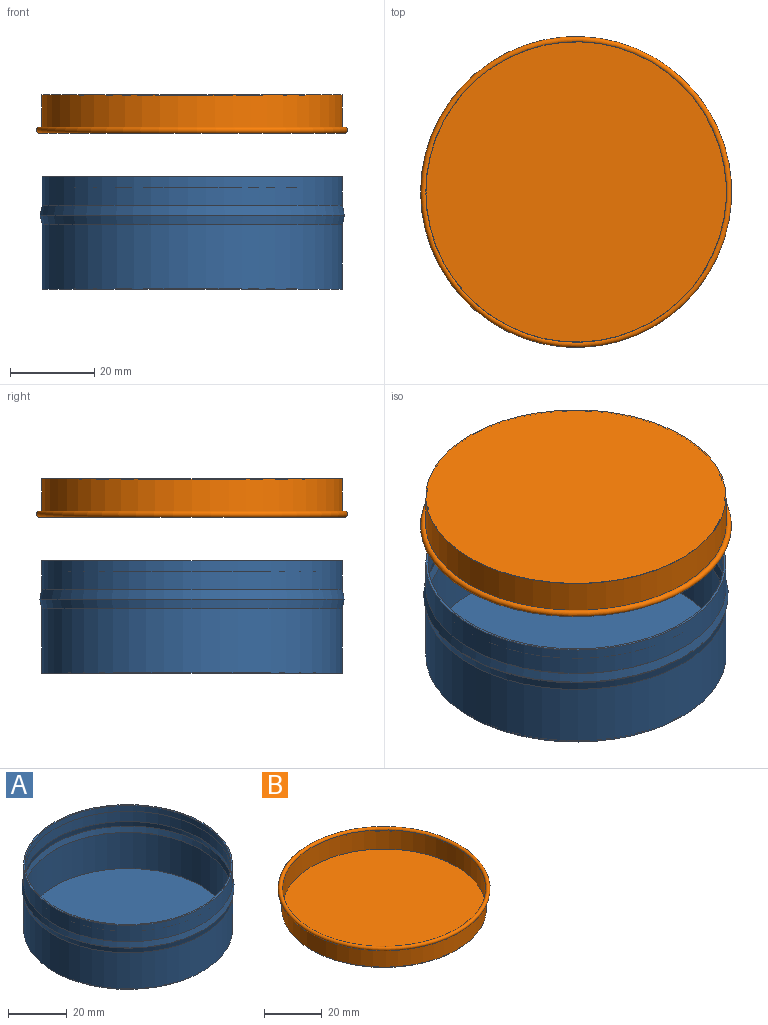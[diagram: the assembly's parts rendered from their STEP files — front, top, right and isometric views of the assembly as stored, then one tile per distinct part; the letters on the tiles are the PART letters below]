
ASSEMBLY  parts=2 mates=1
PART A: 13 faces, bbox 72.1x72.1x26.7 mm
  f0: cylinder r=35.56mm len=71.12mm, axis (0,0,1), area 3405.1mm2, adj f1,f12
  f1: plane 71.12x71.12mm, normal (0,0,-1), area 3972.6mm2, adj f0
  f2: plane 70.61x70.61mm, normal (0,0,1), area 3916mm2, adj f3
  f3: cylinder r=35.31mm len=70.61mm, axis (0,0,1), area 3324.4mm2, adj f2,f4
  f4: cone r=35.31mm half-angle=12.5deg, axis (0,0,1), area 523.2mm2, adj f3,f5
  f5: cone r=35.81mm half-angle=12.5deg, axis (0,0,-1), area 523.2mm2, adj f4,f6
  f6: cylinder r=35.31mm len=70.61mm, axis (0,0,1), area 957.9mm2, adj f5,f7
  f7: cone r=35.31mm half-angle=63.4deg, axis (0,0,-1), area 62.8mm2, adj f6,f8
  f8: cylinder r=35.05mm len=70.1mm, axis (0,0,1), area 531.4mm2, adj f7,f9
  f9: plane 71.12x71.12mm, normal (0,0,1), area 112.7mm2, adj f8,f10
  f10: cylinder r=35.56mm len=71.12mm, axis (0,0,1), area 1532.3mm2, adj f9,f11
  f11: cone r=36.07mm half-angle=12.5deg, axis (0,0,-1), area 527mm2, adj f10,f12
  f12: cone r=35.56mm half-angle=12.5deg, axis (0,0,1), area 527mm2, adj f0,f11
PART B: 7 faces, bbox 79.7x79.7x8.4 mm
  f0: cylinder r=35.56mm len=71.12mm, axis (0,0,1), area 1872.8mm2, adj f1,f6
  f1: plane 71.12x71.12mm, normal (0,0,-1), area 3972.6mm2, adj f0
  f2: plane 70.61x70.61mm, normal (0,0,1), area 3916mm2, adj f3
  f3: cylinder r=35.31mm len=70.61mm, axis (0,0,1), area 1803.1mm2, adj f2,f4
  f4: torus R=36.07mm, axis (0,0,1), area 930.7mm2, adj f3,f5
  f5: cone r=35.6mm half-angle=37.8deg, axis (0,0,1), area 56.9mm2, adj f4,f6
  f6: torus R=36.07mm, axis (0,0,1), area 619.8mm2, adj f0,f5
PLACE A t=(-13.33,10.17,-2.97)mm
PLACE B rot(axis=(0,1,0),180deg) t=(-13.33,10.17,43.04)mm
MATE cylindrical A.f0 <-> B.f0  axis (0,0,1) through (-13.33,10.17,20.27)mm
